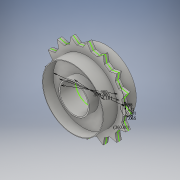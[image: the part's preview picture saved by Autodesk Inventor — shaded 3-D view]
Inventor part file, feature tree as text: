
AUTODESK INVENTOR PART (.ipt)
format: ipt  version: 2016 (Build 200138000, 138)  size: 230,400 bytes
history: native  units: in
note: dims shown in document units (in); Inventor stores cm internally (conversion verified against a paired STEP export)
features: extrude x6, fillet x2, sketch x1
ambient origin geometry x8: Origin, YZ Plane, XZ Plane, XY Plane, X Axis, Y Axis, Z Axis, Center Point
bodies: Solid1 (feature_tree)
feature tree (9):
  sketch  "Sketch1"  dims[d1=1.0in d2=0.98in d3=0.5in d4=0.24in d5=0.24in d6=0.0in d7=0.0in d8=0.27in d9=0.27in d10=0.0in d11=0.0in d12=0.1in d13=0.1in d14=0.0in d15=0.0in d16=0.25in d17=0.25in d18=0.0in d19=0.0in d20=0.001in d21=0.001in d22=1.1811in d24=0.0984in d25=0.0in d26=0.121in d27=0.0651in d28=6.2992in d30=360.0deg d32=0.0787in d33=0.05in d34=0.0in d35=0.0in d36=0.0787in d37=0.0197in d38=0.0in d39=0.0in]
  extrude  "Extrusion1"  Depth=0.0787in
  extrude  "Extrusion2"  Depth=0.5in
  extrude  "Extrusion3"  Depth=0.0787in TaperAngle=0.0deg
  extrude  "Extrusion4"  Depth=0.27in TaperAngle=0.0deg
  fillet  "Fillet1"  Radius=0.1in
  fillet  "Fillet2"  Radius=0.25in
  extrude  "Extrusion5"  Depth=0.0787in
  extrude  "Extrusion6"  Depth=0.0787in
